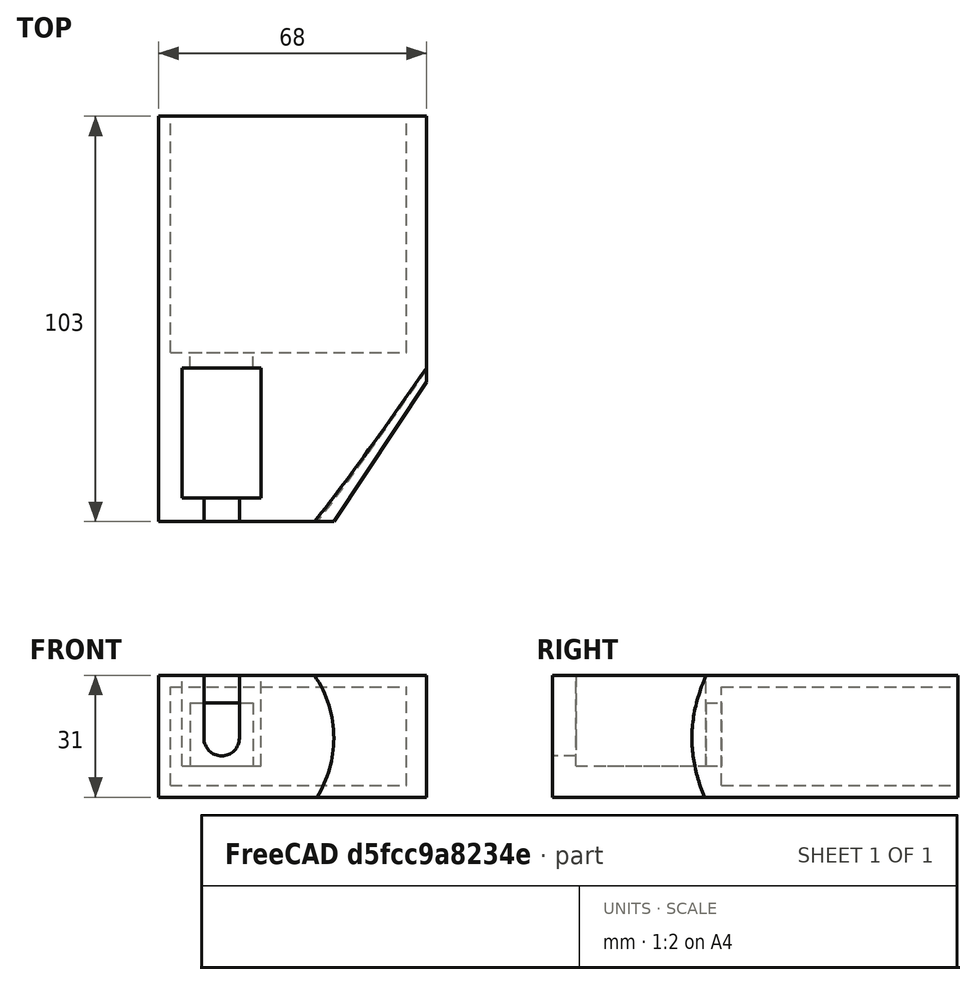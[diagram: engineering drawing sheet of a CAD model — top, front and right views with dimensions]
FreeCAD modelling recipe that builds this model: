
FCSTD DOCUMENT  (FreeCAD 0.15R4671 (Git))
Label: ntpcase
License: All rights reserved
LicenseURL: http://en.wikipedia.org/wiki/All_rights_reserved
objects: Part::Box×10, Part::MultiFuse×3, Part::Cut×3, Part::Cylinder×1, Part::Cone×1, Mesh::Feature×1
note: 18 computed .brp shape members not serialized (recipe doc carries the construction recipe); baked Part::Feature solids carry a one-line shape summary decoded from their .brp

FEATURE [Part::Box] Box  label="thingi"
  Height = 25
  Length = 60
  Placement = pos=(3,3,3) rot=(0,0,1;0rad)
  Width = 60
FEATURE [Part::Box] Box001  label="case"
  Height = 31
  Length = 68
  Width = 63
FEATURE [Part::Box] Box002  label="plughole"
  Height = 16
  Length = 16
  Placement = pos=(8,-26,8) rot=(0,0,1;0rad)
  Width = 33
FEATURE [Part::Cylinder] Cylinder
  Angle = 360
  Height = 80
  Placement = pos=(16,-13,15) rot=(1,0,0;1.5708rad)
  Radius = 4.5
FEATURE [Part::Cone] Cone
  Angle = 360
  Height = 80
  Placement = pos=(16,0,15) rot=(1,0,0;1.5708rad)
  Radius1 = 55
  Radius2 = 2
FEATURE [Part::Box] Box003  label="Cube"
  Height = 48
  Length = 120
  Placement = pos=(-42,-79,-48) rot=(0,0,1;0rad)
  Width = 114
FEATURE [Part::Box] Box004  label="Cube001"
  Height = 48
  Length = 120
  Placement = pos=(-42,-79,31) rot=(0,0,1;0rad)
  Width = 114
FEATURE [Part::Box] Box005  label="Cube002"
  Height = 48
  Length = 42
  Placement = pos=(-42,-79,-9) rot=(0,0,1;0rad)
  Width = 114
FEATURE [Part::Box] Box006  label="Cube003"
  Height = 48
  Length = 45
  Placement = pos=(68,-79,-9) rot=(0,0,1;0rad)
  Width = 116
FEATURE [Part::Box] Box007  label="Cube004"
  Height = 66
  Length = 130
  Placement = pos=(-42,-79,-17) rot=(0,0,1;0rad)
  Width = 39
FEATURE [Part::MultiFuse] Fusion  label="cone-sub"
  Shapes = -> [Box006,Box004,Box007,Box005,Box003]
FEATURE [Part::Cut] Cut
  Base = -> Cone
  Tool = -> Fusion
FEATURE [Part::Cut] Cut001
  Base = -> Box001
  Tool = -> Box
FEATURE [Part::Box] Box008  label="plughole001"
  Height = 26
  Length = 20
  Placement = pos=(6,-34,8) rot=(0,0,1;0rad)
  Width = 33
FEATURE [Part::Box] Box009  label="Cube005"
  Height = 19
  Length = 9
  Placement = pos=(11.5,-66,15) rot=(0,0,1;0rad)
  Width = 35
FEATURE [Part::MultiFuse] Fusion001
  Shapes = -> [Box008,Box002,Box009,Cylinder]
FEATURE [Part::MultiFuse] Fusion002
  Shapes = -> [Cut,Cut001]
FEATURE [Part::Cut] Cut002
  Base = -> Fusion002
  Tool = -> Fusion001
FEATURE [Mesh::Feature] Mesh  label="Cut002 (Meshed)"
